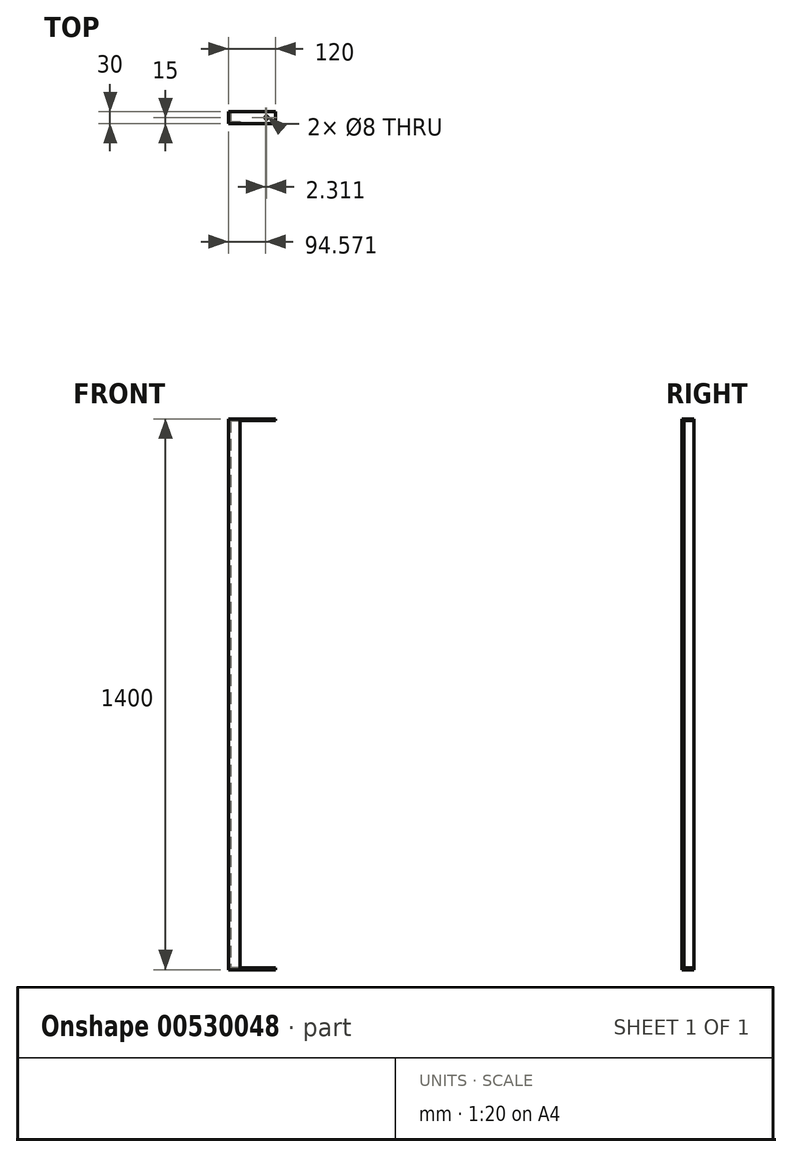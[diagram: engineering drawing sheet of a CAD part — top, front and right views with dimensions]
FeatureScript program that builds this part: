
annotation { "Feature Type Name" : "Feature", "Feature Type Description" : "" }
export const myFeature = defineFeature(function(context is Context, id is Id, definition is map)
    precondition{}
    {
        {
            var Q0;
            Q0=qCreatedBy(makeId("Top.planeOp"),FACE);
            var sketch = newSketch(context, id + "F0", { "sketchPlane" : qUnion([Q0])});
            skLineSegment(sketch, "E0.bottom", {"start": v(60, -15) * mm, "end": v(-60, -15) * mm});
            skLineSegment(sketch, "E0.top", {"start": v(60, 15) * mm, "end": v(-60, 15) * mm});
            skLineSegment(sketch, "E0.left", {"start": v(60, -15) * mm, "end": v(60, 15) * mm});
            skLineSegment(sketch, "E0.right", {"start": v(-60, -15) * mm, "end": v(-60, 15) * mm});
            skPoint(sketch, "E0.middle", {"position": v(0, 0) * mm});
            skSolve(sketch);
        }
        {
            var Q0;
            Q0=makeQuery(id+"F0.imprint","IMPRINT",FACE,{"disambiguationData":[TD([[makeQuery(id+"F0.imprint","IMPRINT",EDGE,{"derivedFrom":sQuery(id+"F0.wireOp",EDGE,"E0.bottom")}),-1.0]])]});
            extrude(context, id + "F1", {"entities" : qUnion([Q0]), "depth" : 5 * mm, "offsetDistance" : 25 * mm});
        }
        {
            var Q0;
            Q0=makeQuery(id+"F1.opExtrude","CAP_FACE",FACE,{"disambiguationData":[OSD([sQuery(id+"F0.wireOp",EDGE,"E0.bottom"),sQuery(id+"F0.wireOp",EDGE,"E0.top"),sQuery(id+"F0.wireOp",EDGE,"E0.left"),sQuery(id+"F0.wireOp",EDGE,"E0.right")])],"isStart":false});
            var sketch = newSketch(context, id + "F2", { "sketchPlane" : qUnion([Q0])});
            skLineSegment(sketch, "E1", {"start": v(-60, 15) * mm, "end": v(-55, 15) * mm});
            skLineSegment(sketch, "E2", {"start": v(-55, 15) * mm, "end": v(-55, -10) * mm});
            skLineSegment(sketch, "E3", {"start": v(-55, -10) * mm, "end": v(-30, -10) * mm});
            skLineSegment(sketch, "E4", {"start": v(-30, -10) * mm, "end": v(-30, -15) * mm});
            skSolve(sketch);
        }
        {
            var Q0;
            Q0 = qSketchRegion(id + "F2", true);
            var Q1;
            Q1=makeQuery(id+"F2.imprint","IMPRINT",FACE,{"disambiguationData":[TD([[makeQuery(id+"F2.imprint","IMPRINT",EDGE,{"derivedFrom":sQuery(id+"F2.wireOp",EDGE,"E1")}),1.0]])]});
            extrude(context, id + "F3", {"entities" : qUnion([Q0, Q1]), "operationType" : NewBodyOperationType.ADD, "depth" : 1390 * mm, "offsetDistance" : 25 * mm});
        }
        {
            var Q0;
            Q0=makeQuery(id+"F3.opExtrude","CAP_FACE",FACE,{"disambiguationData":[OSD([sQuery(id+"F0.wireOp",EDGE,"E0.bottom"),sQuery(id+"F0.wireOp",EDGE,"E0.right"),sQuery(id+"F2.wireOp",EDGE,"E1"),sQuery(id+"F2.wireOp",EDGE,"E2"),sQuery(id+"F2.wireOp",EDGE,"E3"),sQuery(id+"F2.wireOp",EDGE,"E4")])],"isStart":false});
            var sketch = newSketch(context, id + "F4", { "sketchPlane" : qUnion([Q0])});
            skLineSegment(sketch, "E5.bottom", {"start": v(-60, -15) * mm, "end": v(-60, -15) * mm});
            skLineSegment(sketch, "E5.top", {"start": v(-60, 15) * mm, "end": v(-60, 15) * mm});
            skLineSegment(sketch, "E6.bottom", {"start": v(-60, -15) * mm, "end": v(60, -15) * mm});
            skLineSegment(sketch, "E6.top", {"start": v(-60, 15) * mm, "end": v(60, 15) * mm});
            skLineSegment(sketch, "E6.left", {"start": v(-60, -15) * mm, "end": v(-60, 15) * mm});
            skLineSegment(sketch, "E6.right", {"start": v(60, -15) * mm, "end": v(60, 15) * mm});
            skSolve(sketch);
        }
        {
            var Q0;
            {var subQ2=sQuery(id+"F4.wireOp",EDGE,"E6.right");Q0=makeQuery(id+"F4.imprint","IMPRINT",FACE,{"disambiguationData":[TD([[makeQuery(id+"F4.imprint","IMPRINT",EDGE,{"derivedFrom":subQ2}),1.0]])]});}
            var Q1;
            {var subQ0=sQuery(id+"F4.wireOp",EDGE,"E6.left");Q1=makeQuery(id+"F4.imprint","IMPRINT",FACE,{"disambiguationData":[TD([[makeQuery(id+"F4.imprint","IMPRINT",EDGE,{"derivedFrom":subQ0}),-1.0]])]});}
            extrude(context, id + "F5", {"entities" : qUnion([Q0, Q1]), "operationType" : NewBodyOperationType.ADD, "depth" : 5 * mm, "offsetDistance" : 25 * mm});
        }
        {
            var Q0;
            Q0=makeQuery(id+"F5.opExtrude","CAP_FACE",FACE,{"disambiguationData":[OSD([sQuery(id+"F4.wireOp",EDGE,"E6.bottom"),sQuery(id+"F4.wireOp",EDGE,"E6.top"),sQuery(id+"F4.wireOp",EDGE,"E6.left"),sQuery(id+"F4.wireOp",EDGE,"E6.right")])],"isStart":false});
            var sketch = newSketch(context, id + "F6", { "sketchPlane" : qUnion([Q0])});
            skCircle(sketch, "E7", {"center": v(36.88, 0) * mm, "radius": 4 * mm});
            skSolve(sketch);
        }
        {
            var Q0;
            Q0 = qSketchRegion(id + "F6", true);
            extrude(context, id + "F7", {"entities" : qUnion([Q0]), "operationType" : NewBodyOperationType.REMOVE, "oppositeDirection" : true, "depth" : 25 * mm, "offsetDistance" : 25 * mm});
        }
        {
            var Q0;
            Q0=makeQuery(id+"F1.opExtrude","CAP_FACE",FACE,{"disambiguationData":[OSD([sQuery(id+"F0.wireOp",EDGE,"E0.bottom"),sQuery(id+"F0.wireOp",EDGE,"E0.top"),sQuery(id+"F0.wireOp",EDGE,"E0.left"),sQuery(id+"F0.wireOp",EDGE,"E0.right")])],"isStart":false});
            var sketch = newSketch(context, id + "F8", { "sketchPlane" : qUnion([Q0])});
            skCircle(sketch, "E8", {"center": v(34.57, 0) * mm, "radius": 4 * mm});
            skSolve(sketch);
        }
        {
            var Q0;
            Q0 = qSketchRegion(id + "F8", true);
            extrude(context, id + "F9", {"entities" : qUnion([Q0]), "operationType" : NewBodyOperationType.REMOVE, "oppositeDirection" : true, "depth" : 25 * mm, "offsetDistance" : 25 * mm});
        }
    });
